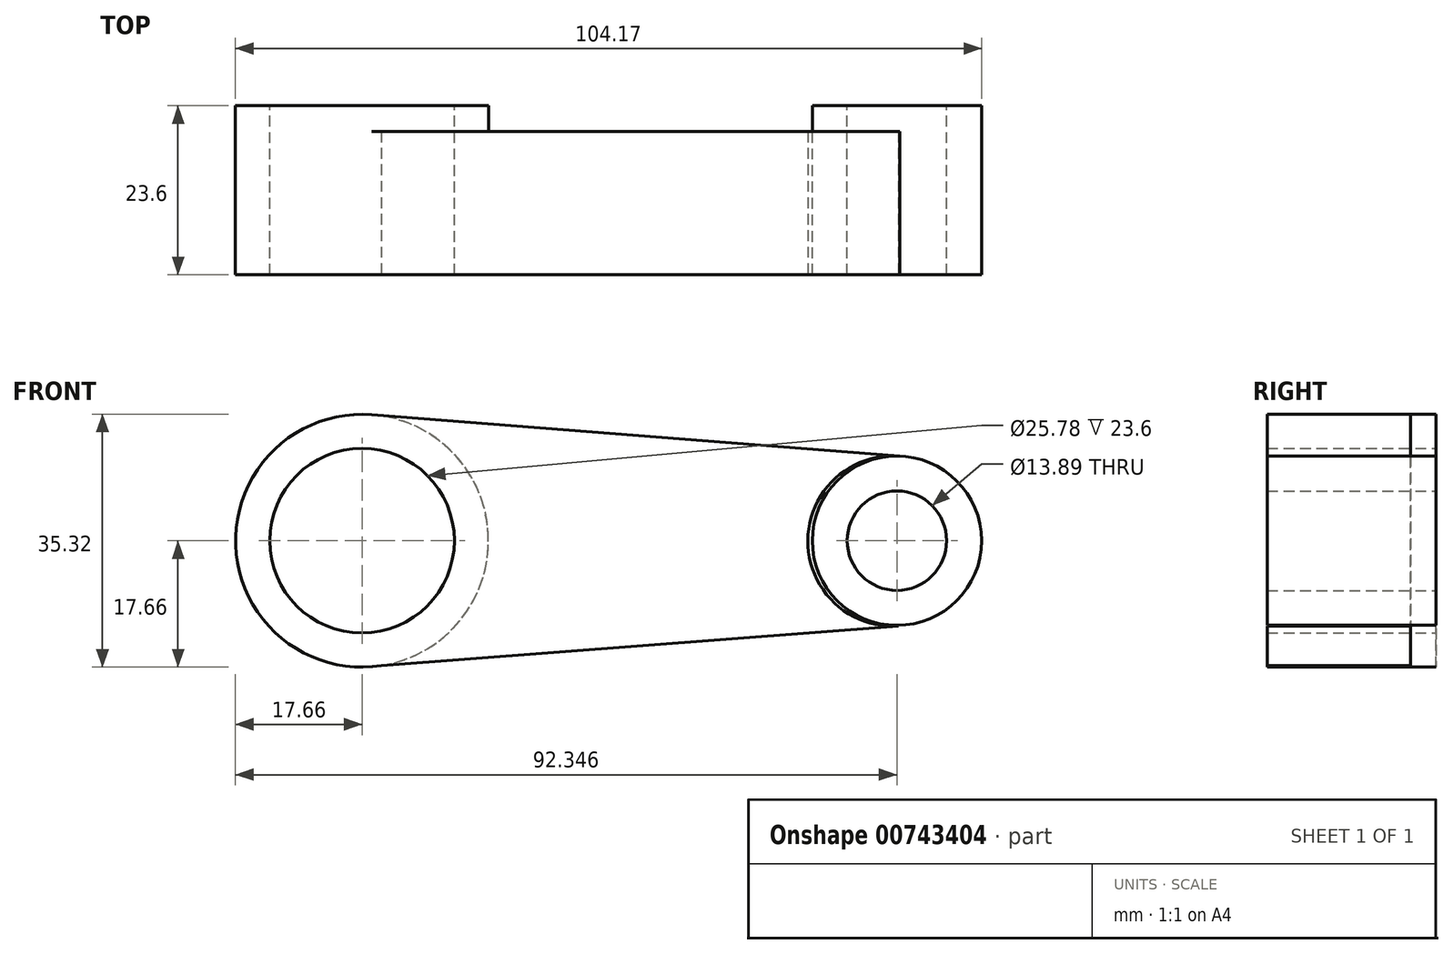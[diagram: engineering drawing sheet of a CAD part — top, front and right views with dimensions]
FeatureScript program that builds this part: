
annotation { "Feature Type Name" : "Feature", "Feature Type Description" : "" }
export const myFeature = defineFeature(function(context is Context, id is Id, definition is map)
    precondition{}
    {
        {
            var Q0;
            Q0=qCreatedBy(makeId("Front.planeOp"),FACE);
            var sketch = newSketch(context, id + "F0", { "sketchPlane" : qUnion([Q0])});
            skCircle(sketch, "E0", {"center": v(0, 0) * mm, "radius": 12.9 * mm});
            skCircle(sketch, "E1", {"center": v(0, 0) * mm, "radius": 17.66 * mm});
            skCircle(sketch, "E2", {"center": v(74.69, 0) * mm, "radius": 6.94 * mm});
            skCircle(sketch, "E3", {"center": v(74.69, 0) * mm, "radius": 11.82 * mm});
            skSolve(sketch);
        }
        {
            var Q0;
            Q0=makeQuery(id+"F0.imprint","IMPRINT",FACE,{"disambiguationData":[TD([[makeQuery(id+"F0.imprint","IMPRINT",EDGE,{"derivedFrom":sQuery(id+"F0.wireOp",EDGE,"E2")}),-1.0]])]});
            var Q1;
            Q1=makeQuery(id+"F0.imprint","IMPRINT",FACE,{"disambiguationData":[TD([[makeQuery(id+"F0.imprint","IMPRINT",EDGE,{"derivedFrom":sQuery(id+"F0.wireOp",EDGE,"E0")}),-1.0]])]});
            extrude(context, id + "F1", {"entities" : qUnion([Q0, Q1]), "depth" : 23.6 * mm, "offsetDistance" : 25 * mm});
        }
        {
            var Q0;
            Q0=makeQuery(id+"F1.opExtrude","CAP_FACE",FACE,{"disambiguationData":[OSD([sQuery(id+"F0.wireOp",EDGE,"E0"),sQuery(id+"F0.wireOp",EDGE,"E1")])],"isStart":false});
            var sketch = newSketch(context, id + "F2", { "sketchPlane" : qUnion([Q0])});
            skLineSegment(sketch, "E4", {"start": v(75.08, 11.82) * mm, "end": v(0, 17.71) * mm});
            skLineSegment(sketch, "E5", {"start": v(0, -17.66) * mm, "end": v(74.9, -11.93) * mm});
            skArc(sketch, "E6", {"start": v(75.08, 11.82) * mm, "mid": v(62.24, 0.04) * mm, "end": v(74.9, -11.93) * mm});
            skSolve(sketch);
        }
        {
            var Q0;
            Q0 = qSketchRegion(id + "F2", true);
            var Q1;
            {var subQ0=sQuery(id+"F2.wireOp",EDGE,"E6");Q1=makeQuery(id+"F2.imprint","IMPRINT",FACE,{"disambiguationData":[TD([[makeQuery(id+"F2.imprint","IMPRINT",EDGE,{"derivedFrom":subQ0}),-1.0]])]});}
            extrude(context, id + "F3", {"entities" : qUnion([Q0, Q1]), "operationType" : NewBodyOperationType.ADD, "oppositeDirection" : true, "depth" : 20 * mm, "offsetDistance" : 25 * mm});
        }
    });
